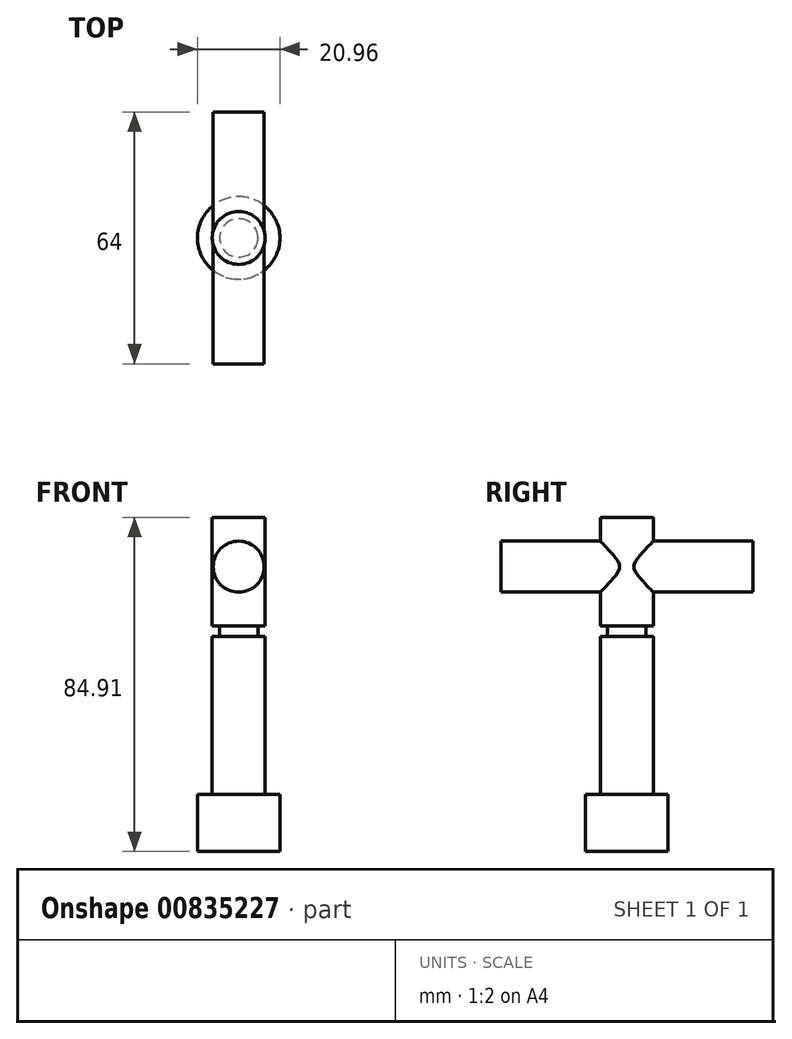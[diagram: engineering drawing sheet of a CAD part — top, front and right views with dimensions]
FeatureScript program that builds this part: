
annotation { "Feature Type Name" : "Feature", "Feature Type Description" : "" }
export const myFeature = defineFeature(function(context is Context, id is Id, definition is map)
    precondition{}
    {
        {
            var Q0;
            Q0=qCreatedBy(makeId("Front.planeOp"),FACE);
            var sketch = newSketch(context, id + "F0", { "sketchPlane" : qUnion([Q0])});
            skLineSegment(sketch, "E0", {"start": v(0, 55.43) * mm, "end": v(6.72, 55.43) * mm});
            skLineSegment(sketch, "E1", {"start": v(6.72, 55.43) * mm, "end": v(6.72, 48.06) * mm});
            skLineSegment(sketch, "E2", {"start": v(0, 0) * mm, "end": v(0, 55.43) * mm});
            skLineSegment(sketch, "E3", {"start": v(0, 0) * mm, "end": v(0, -21.73) * mm});
            skLineSegment(sketch, "E4", {"start": v(6.72, 42.35) * mm, "end": v(6.72, 27.8) * mm});
            skLineSegment(sketch, "E5", {"start": v(6.72, 27.8) * mm, "end": v(4.88, 27.8) * mm});
            skLineSegment(sketch, "E6", {"start": v(4.88, 25.23) * mm, "end": v(6.72, 25.23) * mm});
            skLineSegment(sketch, "E7", {"start": v(6.72, 25.23) * mm, "end": v(6.72, -14.92) * mm});
            skLineSegment(sketch, "E8", {"start": v(6.72, -14.92) * mm, "end": v(10.48, -14.92) * mm});
            skLineSegment(sketch, "E9", {"start": v(10.48, -14.92) * mm, "end": v(10.48, -29.48) * mm});
            skLineSegment(sketch, "E10", {"start": v(0, 25.23) * mm, "end": v(0, 27.8) * mm});
            skLineSegment(sketch, "E11", {"start": v(10.48, -29.48) * mm, "end": v(0, -29.48) * mm});
            skLineSegment(sketch, "E12", {"start": v(0, -29.48) * mm, "end": v(0, -21.73) * mm});
            skLineSegment(sketch, "E13", {"start": v(4.88, 25.23) * mm, "end": v(4.88, 27.8) * mm});
            skLineSegment(sketch, "E14", {"start": v(6.72, 42.35) * mm, "end": v(6.72, 48.06) * mm});
            skSolve(sketch);
        }
        {
            var Q0;
            {var subQ2=sQuery(id+"F0.wireOp",EDGE,"E0");Q0=makeQuery(id+"F0.imprint","IMPRINT",FACE,{"disambiguationData":[TD([[makeQuery(id+"F0.imprint","IMPRINT",EDGE,{"derivedFrom":subQ2}),-1.0]])]});}
            var Q1;
            Q1=sQuery(id+"F0.wireOp",EDGE,"E2");
            revolve(context, id + "F1", {"surfaceOperationType" : NewSurfaceOperationType.NEW, "entities" : qUnion([Q0]), "axis" : qUnion([Q1]), "revolveType" : RevolveType.FULL});
        }
        {
            var Q0;
            Q0=qCreatedBy(makeId("Front.planeOp"),FACE);
            var sketch = newSketch(context, id + "F2", { "sketchPlane" : qUnion([Q0])});
            skCircle(sketch, "E15", {"center": v(0, 42.9) * mm, "radius": 6.48 * mm});
            skSolve(sketch);
        }
        {
            var Q0;
            Q0 = qSketchRegion(id + "F2", true);
            extrude(context, id + "F3", {"entities" : qUnion([Q0]), "operationType" : NewBodyOperationType.ADD, "depth" : 32 * mm, "offsetDistance" : 25.4 * mm, "hasSecondDirection" : true, "secondDirectionOppositeDirection" : true, "secondDirectionDepth" : 32 * mm});
        }
    });
